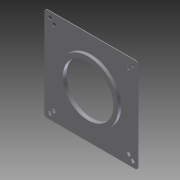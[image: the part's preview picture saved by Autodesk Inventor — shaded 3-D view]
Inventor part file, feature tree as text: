
AUTODESK INVENTOR PART (.ipt)
format: ipt  version: 2011 (Build 150239000, 239)  size: 145,920 bytes
history: native  units: in
note: dims shown in document units (in); Inventor stores cm internally (conversion verified against a paired STEP export)
features: extrude x8, sketch x8, fillet x1
ambient origin geometry x8: Origin, YZ Plane, XZ Plane, XY Plane, X Axis, Y Axis, Z Axis, Center Point
bodies: Solid1 (feature_tree)
feature tree (17):
  extrude  "Extrusion1"  Depth=4.0in
  extrude  "Extrusion2"  Depth=2.16in
  extrude  "Extrusion3"  Depth=1.7655in
  extrude  "Extrusion4"  Depth=0.029in TaperAngle=0.0deg
  extrude  "Extrusion5"  Depth=2.36in
  fillet  "Fillet1"  Radius=2.56in
  extrude  "Extrusion6"  Depth=0.125in
  extrude  "Extrusion7"  Depth=0.131in TaperAngle=0.0deg
  extrude  "Extrusion8"  Depth=0.156in
  sketch  "Sketch1"  dims[d0=4.0in d1=4.0in]
  sketch  "Sketch2"  dims[d2=0.029in d3=0.0in d4=2.16in]
  sketch  "Sketch3"  dims[d5=0.029in d6=0.0in d7=1.7655in]
  sketch  "Sketch4"  dims[d8=0.156in d9=0.029in d10=0.0in]
  sketch  "Sketch5"  dims[d11=0.029in d12=0.0in d13=2.36in d14=2.56in]
  sketch  "Sketch6"  dims[d15=0.262in d16=0.0in d17=0.125in]
  sketch  "Sketch7"  dims[d18=0.131in d19=0.0in d20=0.131in d21=0.0in]
  sketch  "Sketch8"  dims[d22=1.594in d23=0.156in d24=0.131in d25=0.0in]
